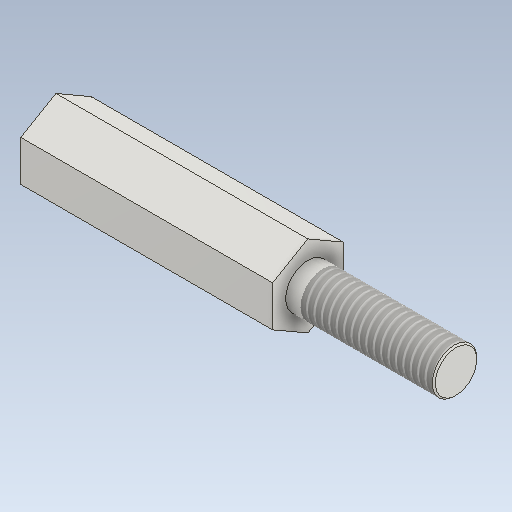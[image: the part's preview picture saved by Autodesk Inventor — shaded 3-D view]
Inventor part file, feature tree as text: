
AUTODESK INVENTOR PART (.ipt)
format: ipt  version: 2021 (Build 250183000, 183)  size: 141,312 bytes
history: native  units: mm
features: other x5, thread x4, chamfer x2, revolve x1
ambient origin geometry x6: Origin, XZ Plane, XY Plane, X Axis, Y Axis, Z Axis
bodies: Solid1 (feature_tree)
feature tree (12):
  revolve  "Revolution1"  [1 undecoded]
  other  "N-Side1"
  thread  "Thread5"  [1 undecoded]
  thread  "Thread7"  [1 undecoded]
  other  "Start Plane"
  other  "Origin point"
  other  "Main Sketch"
  other  "iFeature1:1"
  thread  "Thread4"  [1 undecoded]
  chamfer  "Chamfer3"  [1 undecoded]
  thread  "Thread6"  [1 undecoded]
  chamfer  "Chamfer4"  Distance=0.1mm Angle=45.0deg
note: 6 required parameter values undecoded (feature->parameter linkage not recoverable at this tier; creation-order binding heuristic only, values carry confidence <= 0.55)